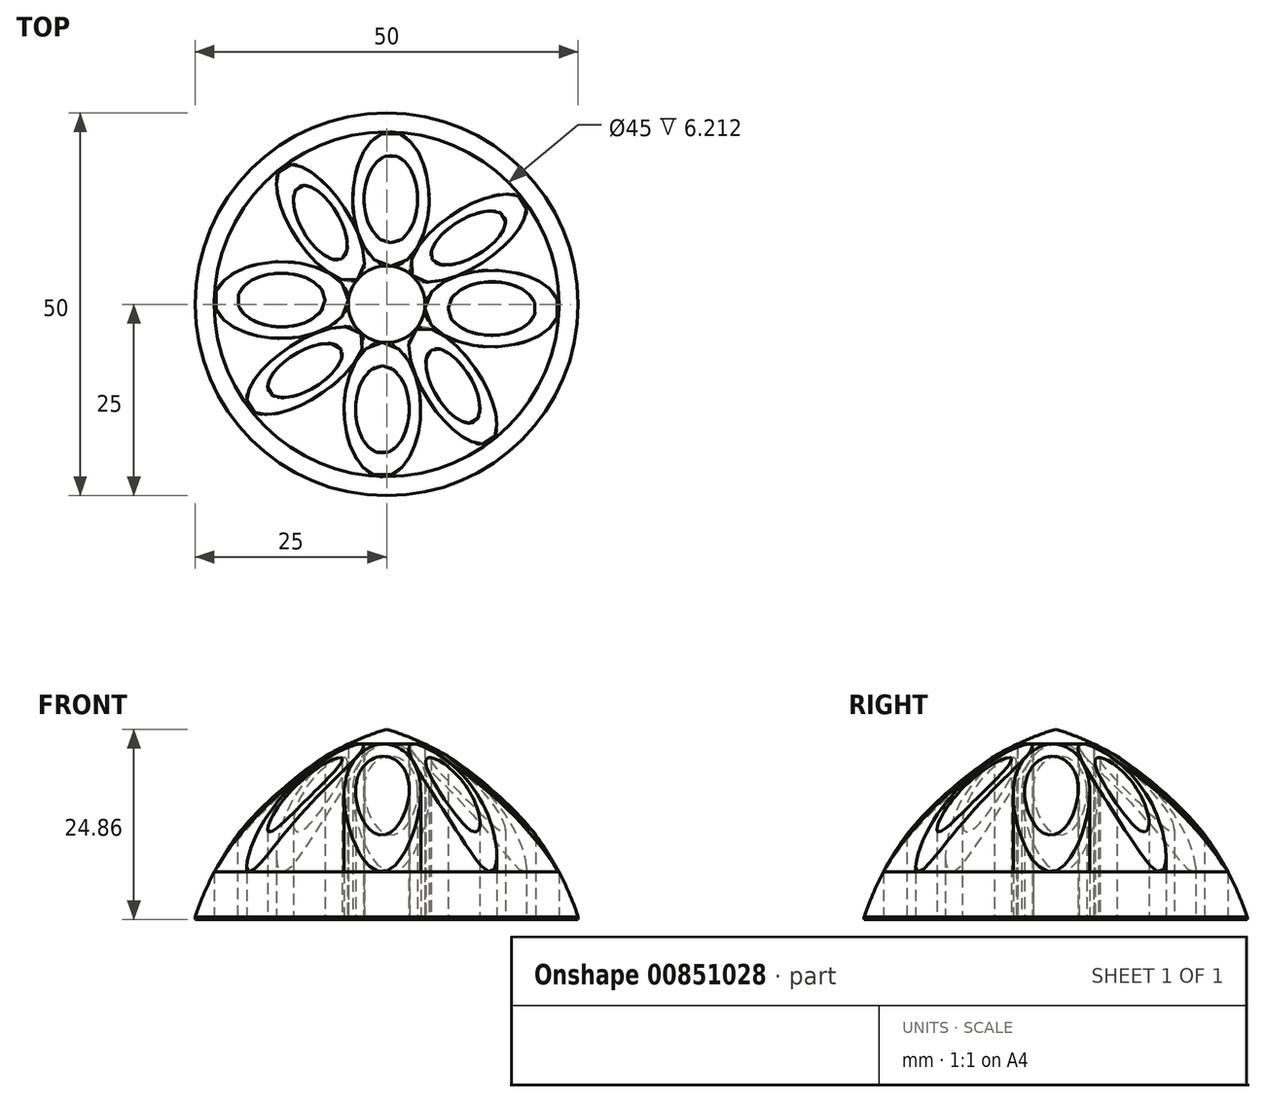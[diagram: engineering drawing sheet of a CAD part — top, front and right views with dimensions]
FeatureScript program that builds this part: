
annotation { "Feature Type Name" : "Feature", "Feature Type Description" : "" }
export const myFeature = defineFeature(function(context is Context, id is Id, definition is map)
    precondition{}
    {
        {
            var Q0;
            Q0=qCreatedBy(makeId("Top.planeOp"),FACE);
            var sketch = newSketch(context, id + "F0", { "sketchPlane" : qUnion([Q0])});
            skCircle(sketch, "E0", {"center": v(0, 0) * mm, "radius": 25 * mm});
            skCircle(sketch, "E1", {"center": v(0, 0) * mm, "radius": 22.5 * mm});
            skCircle(sketch, "E2", {"center": v(0, 0) * mm, "radius": 5 * mm});
            skSolve(sketch);
        }
        {
            var Q0;
            Q0=makeQuery(id+"F0.imprint","IMPRINT",FACE,{"disambiguationData":[TD([[makeQuery(id+"F0.imprint","IMPRINT",EDGE,{"derivedFrom":sQuery(id+"F0.wireOp",EDGE,"E0")}),1.0]])]});
            var Q1;
            Q1=makeQuery(id+"F0.imprint","IMPRINT",FACE,{"disambiguationData":[TD([[makeQuery(id+"F0.imprint","IMPRINT",EDGE,{"derivedFrom":sQuery(id+"F0.wireOp",EDGE,"E2")}),1.0]])]});
            extrude(context, id + "F1", {"entities" : qUnion([Q0, Q1]), "depth" : 25 * mm, "offsetDistance" : 25 * mm});
        }
        {
            var Q0;
            Q0=qCreatedBy(makeId("Top.planeOp"),FACE);
            var sketch = newSketch(context, id + "F2", { "sketchPlane" : qUnion([Q0])});
            skEllipse(sketch, "E3", {"center": v(-13.74, 0.56) * mm, "majorRadius": 8.76 * mm, "minorRadius": 5 * mm, "majorAxis": v(1, 0)});
            skEllipse(sketch, "E4", {"center": v(-13.74, 0.56) * mm, "majorRadius": 5.72 * mm, "minorRadius": 3.5 * mm, "majorAxis": v(1, 0)});
            skEllipse(sketch, "E5", {"center": v(13.75, 0) * mm, "majorRadius": 8.75 * mm, "minorRadius": 5 * mm, "majorAxis": v(1, 0)});
            skEllipse(sketch, "E6", {"center": v(13.75, 0) * mm, "majorRadius": 5.72 * mm, "minorRadius": 3.5 * mm, "majorAxis": v(1, 0)});
            skSolve(sketch);
        }
        {
            var Q0;
            Q0=makeQuery(id+"F2.imprint","IMPRINT",FACE,{"disambiguationData":[TD([[makeQuery(id+"F2.imprint","IMPRINT",EDGE,{"derivedFrom":sQuery(id+"F2.wireOp",EDGE,"E3")}),1.0]])]});
            extrude(context, id + "F3", {"entities" : qUnion([Q0]), "depth" : 25 * mm, "offsetDistance" : 25 * mm});
        }
        {
            var Q0;
            Q0=makeQuery(id+"F3.opExtrude","SWEPT_BODY",BODY,{"disambiguationData":[OSD([sQuery(id+"F2.wireOp",EDGE,"E3"),sQuery(id+"F2.wireOp",EDGE,"E4")])]});
            var Q1;
            Q1=makeQuery(id+"F1.opExtrude","CAP_EDGE",EDGE,{"disambiguationData":[OSD([sQuery(id+"F0.wireOp",EDGE,"E2")])],"isStart":false});
            circularPattern(context, id + "F4", {"entities" : qUnion([Q0]), "axis" : qUnion([Q1]), "angle" : 360 * degree, "instanceCount" : 4, "equalSpace" : true});
        }
        {
            var Q0;
            Q0=qCreatedBy(makeId("Top.planeOp"),FACE);
            var sketch = newSketch(context, id + "F5", { "sketchPlane" : qUnion([Q0])});
            skEllipse(sketch, "E7", {"center": v(-10.65, -8.65) * mm, "majorRadius": 8.8 * mm, "minorRadius": 3.7 * mm, "majorAxis": v(0.83, 0.55)});
            skEllipse(sketch, "E8", {"center": v(-10.65, -8.65) * mm, "majorRadius": 5.47 * mm, "minorRadius": 2.5 * mm, "majorAxis": v(0.86, 0.51)});
            skSolve(sketch);
        }
        {
            var Q0;
            Q0=makeQuery(id+"F5.imprint","IMPRINT",FACE,{"disambiguationData":[TD([[makeQuery(id+"F5.imprint","IMPRINT",EDGE,{"derivedFrom":sQuery(id+"F5.wireOp",EDGE,"E7")}),1.0]])]});
            extrude(context, id + "F6", {"entities" : qUnion([Q0]), "depth" : 25 * mm, "offsetDistance" : 25 * mm});
        }
        {
            var Q0;
            Q0=makeQuery(id+"F6.opExtrude","SWEPT_BODY",BODY,{"disambiguationData":[OSD([sQuery(id+"F5.wireOp",EDGE,"E7"),sQuery(id+"F5.wireOp",EDGE,"E8")])]});
            var Q1;
            Q1=makeQuery(id+"F1.opExtrude","CAP_EDGE",EDGE,{"disambiguationData":[OSD([sQuery(id+"F0.wireOp",EDGE,"E2")])],"isStart":false});
            circularPattern(context, id + "F7", {"entities" : qUnion([Q0]), "axis" : qUnion([Q1]), "angle" : 360 * degree, "instanceCount" : 4, "equalSpace" : true});
        }
        {
            var Q0;
            Q0=qCreatedBy(makeId("Front.planeOp"),FACE);
            var sketch = newSketch(context, id + "F8", { "sketchPlane" : qUnion([Q0])});
            skArc(sketch, "E9", {"start": v(25.11, 0) * mm, "mid": v(15.6, 15.5) * mm, "end": v(0, 24.86) * mm});
            skLineSegment(sketch, "E10", {"start": v(0, 24.86) * mm, "end": v(0, 33.93) * mm});
            skLineSegment(sketch, "E11", {"start": v(0, 33.93) * mm, "end": v(29.4, 33.93) * mm});
            skLineSegment(sketch, "E12", {"start": v(29.4, 33.93) * mm, "end": v(29.4, 0) * mm});
            skLineSegment(sketch, "E13", {"start": v(29.4, 0) * mm, "end": v(25.11, 0) * mm});
            skSolve(sketch);
        }
        {
            var Q0;
            Q0 = qSketchRegion(id + "F8", true);
            var Q1;
            Q1=sQuery(id+"F8.wireOp",EDGE,"E10");
            revolve(context, id + "F9", {"operationType" : NewBodyOperationType.REMOVE, "surfaceOperationType" : NewSurfaceOperationType.NEW, "entities" : qUnion([Q0]), "axis" : qUnion([Q1]), "revolveType" : RevolveType.FULL, "oppositeDirection" : true});
        }
    });
